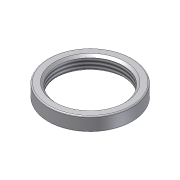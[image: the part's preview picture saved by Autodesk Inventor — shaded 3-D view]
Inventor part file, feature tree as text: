
AUTODESK INVENTOR PART (.ipt)
format: ipt  version: unknown  size: 187,904 bytes
history: native  units: mm (DEFAULTED — no unit token found)
features: extrude x1, thread x1, chamfer x1, fillet x1, sketch x1
ambient origin geometry x8: Origin, YZ Plane, XZ Plane, XY Plane, X Axis, Y Axis, Z Axis, Center Point
feature tree (5):
  extrude  "Extrusion1"  Depth=29.0mm
  thread  "Thread1"  [1 undecoded]
  chamfer  "Chamfer1"  Distance=0.5mm
  fillet  "Fillet1"  [1 undecoded]
  sketch  "Sketch1"  dims[d0=37.0mm d1=29.0mm d2=6.2mm d3=0.0mm d4=10.0mm d5=0.0mm d6=1.0mm d7=2.0mm d8=45.0deg d9=0.5mm]
note: 2 required parameter values undecoded (feature->parameter linkage not recoverable at this tier; creation-order binding heuristic only, values carry confidence <= 0.55)
